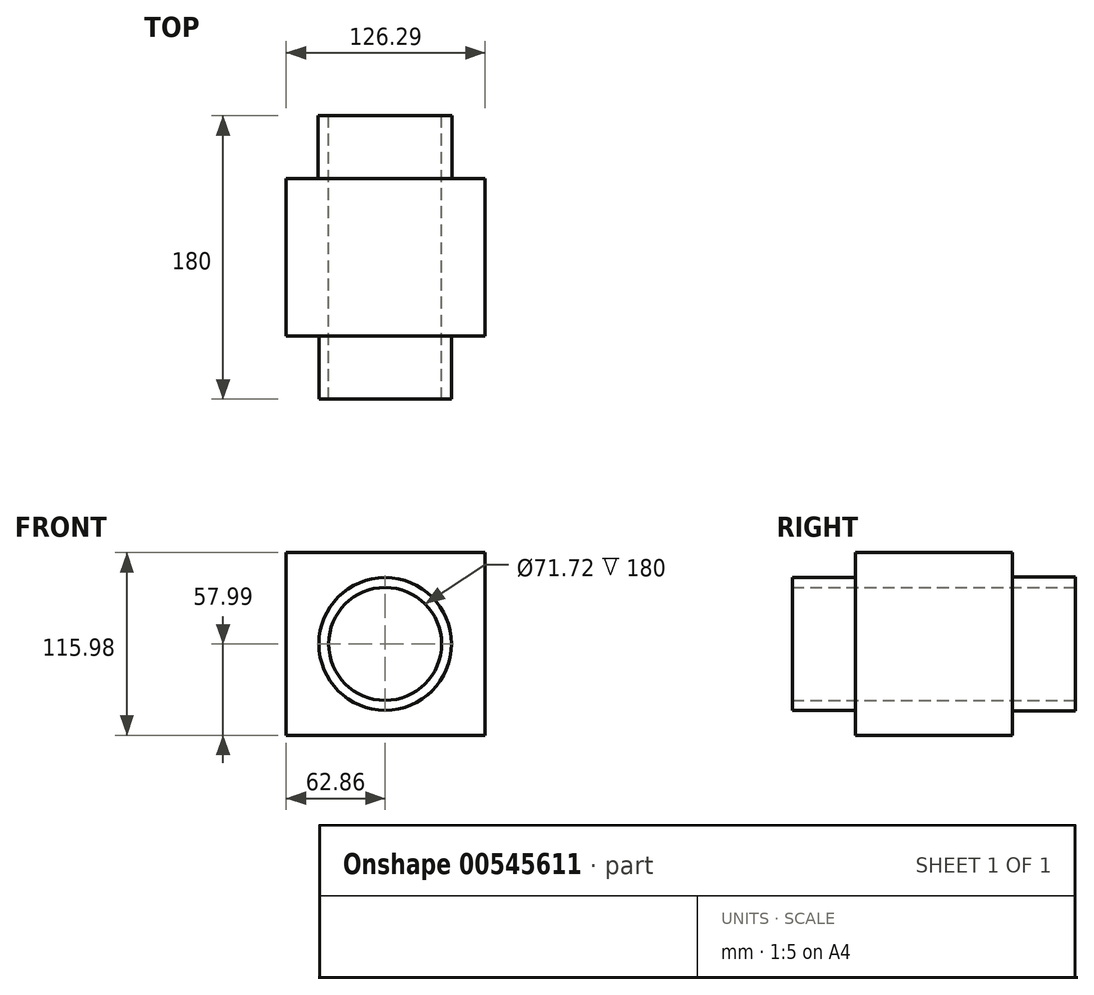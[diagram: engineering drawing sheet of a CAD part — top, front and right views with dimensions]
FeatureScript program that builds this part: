
annotation { "Feature Type Name" : "Feature", "Feature Type Description" : "" }
export const myFeature = defineFeature(function(context is Context, id is Id, definition is map)
    precondition{}
    {
        {
            var Q0;
            Q0=qCreatedBy(makeId("Front.planeOp"),FACE);
            var sketch = newSketch(context, id + "F0", { "sketchPlane" : qUnion([Q0])});
            skLineSegment(sketch, "E0.bottom", {"start": v(-62.86, 57.99) * mm, "end": v(63.43, 57.99) * mm});
            skLineSegment(sketch, "E0.top", {"start": v(-62.86, -57.99) * mm, "end": v(63.43, -57.99) * mm});
            skLineSegment(sketch, "E0.left", {"start": v(-62.86, 57.99) * mm, "end": v(-62.86, -57.99) * mm});
            skLineSegment(sketch, "E0.right", {"start": v(63.43, 57.99) * mm, "end": v(63.43, -57.99) * mm});
            skCircle(sketch, "E1", {"center": v(0, 0) * mm, "radius": 35.86 * mm});
            skCircle(sketch, "E2", {"center": v(0, 0) * mm, "radius": 30.62 * mm});
            skSolve(sketch);
        }
        {
            var Q0;
            Q0=makeQuery(id+"F0.imprint","IMPRINT",FACE,{"disambiguationData":[TD([[makeQuery(id+"F0.imprint","IMPRINT",EDGE,{"derivedFrom":sQuery(id+"F0.wireOp",EDGE,"E0.bottom")}),-1.0]])]});
            extrude(context, id + "F1", {"entities" : qUnion([Q0]), "depth" : 100 * mm, "offsetDistance" : 25 * mm});
        }
        {
            var Q0;
            Q0=makeQuery(id+"F1.opExtrude","CAP_FACE",FACE,{"disambiguationData":[OSD([sQuery(id+"F0.wireOp",EDGE,"E0.bottom"),sQuery(id+"F0.wireOp",EDGE,"E0.top"),sQuery(id+"F0.wireOp",EDGE,"E0.left"),sQuery(id+"F0.wireOp",EDGE,"E0.right"),sQuery(id+"F0.wireOp",EDGE,"E1")])],"isStart":false});
            var sketch = newSketch(context, id + "F2", { "sketchPlane" : qUnion([Q0])});
            skCircle(sketch, "E3", {"center": v(0, 0) * mm, "radius": 42.12 * mm});
            skSolve(sketch);
        }
        {
            var Q0;
            Q0=makeQuery(id+"F2.imprint","IMPRINT",FACE,{"disambiguationData":[TD([[makeQuery(id+"F2.imprint","IMPRINT",EDGE,{"derivedFrom":sQuery(id+"F2.wireOp",EDGE,"E3")}),1.0]])]});
            extrude(context, id + "F3", {"entities" : qUnion([Q0]), "operationType" : NewBodyOperationType.ADD, "depth" : 40 * mm, "offsetDistance" : 25 * mm});
        }
        {
            var Q0;
            Q0=makeQuery(id+"F1.opExtrude","CAP_FACE",FACE,{"disambiguationData":[OSD([sQuery(id+"F0.wireOp",EDGE,"E0.bottom"),sQuery(id+"F0.wireOp",EDGE,"E0.top"),sQuery(id+"F0.wireOp",EDGE,"E0.left"),sQuery(id+"F0.wireOp",EDGE,"E0.right"),sQuery(id+"F0.wireOp",EDGE,"E1")])],"isStart":true});
            var sketch = newSketch(context, id + "F4", { "sketchPlane" : qUnion([Q0])});
            skCircle(sketch, "E4", {"center": v(0, 0) * mm, "radius": 42.48 * mm});
            skSolve(sketch);
        }
        {
            var Q0;
            Q0=makeQuery(id+"F4.imprint","IMPRINT",FACE,{"disambiguationData":[TD([[makeQuery(id+"F4.imprint","IMPRINT",EDGE,{"derivedFrom":sQuery(id+"F4.wireOp",EDGE,"E4")}),1.0]])]});
            extrude(context, id + "F5", {"entities" : qUnion([Q0]), "operationType" : NewBodyOperationType.ADD, "depth" : 40 * mm, "offsetDistance" : 25 * mm});
        }
    });
